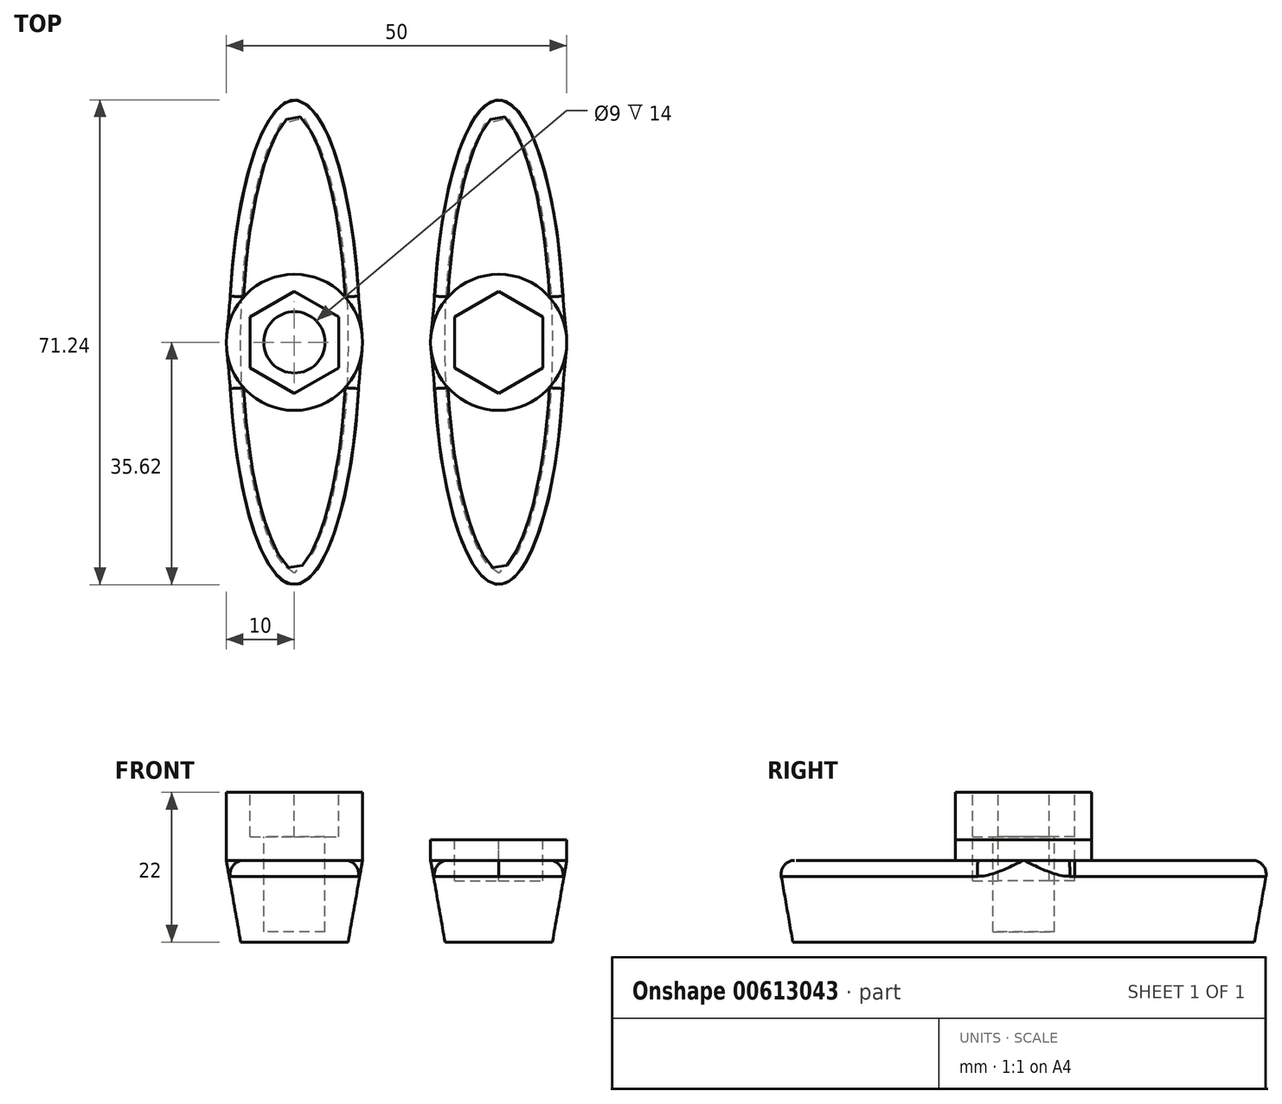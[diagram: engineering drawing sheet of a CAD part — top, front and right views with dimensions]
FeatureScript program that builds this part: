
annotation { "Feature Type Name" : "Feature", "Feature Type Description" : "" }
export const myFeature = defineFeature(function(context is Context, id is Id, definition is map)
    precondition{}
    {
        {
            var Q0;
            Q0=qCreatedBy(makeId("Top.planeOp"),FACE);
            var sketch = newSketch(context, id + "F0", { "sketchPlane" : qUnion([Q0])});
            skEllipse(sketch, "E0", {"center": v(0, 0) * mm, "majorRadius": 36 * mm, "minorRadius": 10 * mm, "majorAxis": v(0, 1)});
            skSolve(sketch);
        }
        {
            var Q0;
            Q0=makeQuery(id+"F0.imprint","IMPRINT",FACE,{"disambiguationData":[TD([[makeQuery(id+"F0.imprint","IMPRINT",EDGE,{"derivedFrom":sQuery(id+"F0.wireOp",EDGE,"E0")}),1.0]])]});
            extrude(context, id + "F1", {"entities" : qUnion([Q0]), "oppositeDirection" : true, "depth" : 12 * mm, "offsetDistance" : 25 * mm, "hasDraft" : true, "draftAngle" : 10 * degree, "draftPullDirection" : true});
        }
        {
            var Q0;
            Q0=makeQuery(id+"F1.opExtrude","SWEPT_BODY",BODY,{"disambiguationData":[OSD([sQuery(id+"F0.wireOp",EDGE,"E0")])]});
            transform(context, id + "F2", {"entities" : qUnion([Q0]), "transformType" : TransformType.TRANSLATION_3D, "dx" : 30 * mm, "dy" : 0 * mm, "dz" : 0 * mm, "makeCopy" : true});
        }
        {
            var Q0;
            Q0=makeQuery(id+"F1.opExtrude","CAP_FACE",FACE,{"disambiguationData":[OSD([sQuery(id+"F0.wireOp",EDGE,"E0")])],"isStart":true});
            var sketch = newSketch(context, id + "F3", { "sketchPlane" : qUnion([Q0])});
            skCircle(sketch, "E1", {"center": v(0, 0) * mm, "radius": 10 * mm});
            skSolve(sketch);
        }
        {
            var Q0;
            {var subQ0=sQuery(id+"F3.wireOp",EDGE,"E1");var subQ1=makeQuery(id+"F1.opExtrude","CAP_EDGE",EDGE,{"disambiguationData":[OSD([sQuery(id+"F0.wireOp",EDGE,"E0")])],"isStart":true});var subQ2=makeQuery(id+"F3.imprint","INTERSECT",VERTEX,{"disambiguationData":[OD(0.0)],"derivedFrom":[subQ1,subQ0]});Q0=makeQuery(id+"F3.imprint","IMPRINT",FACE,{"disambiguationData":[TD([[makeQuery(id+"F3.imprint","IMPRINT",EDGE,{"disambiguationData":[TD([[subQ2,1.0]])],"derivedFrom":subQ0}),1.0]])]});}
            extrude(context, id + "F4", {"entities" : qUnion([Q0]), "operationType" : NewBodyOperationType.ADD, "depth" : 10 * mm, "offsetDistance" : 25 * mm});
        }
        {
            var Q0;
            Q0=makeQuery(id+"F2.opPattern","COPY",FACE,{"derivedFrom":makeQuery(id+"F1.opExtrude","CAP_FACE",FACE,{"disambiguationData":[OSD([sQuery(id+"F0.wireOp",EDGE,"E0")])],"isStart":true}),"instanceName":"1"});
            var sketch = newSketch(context, id + "F5", { "sketchPlane" : qUnion([Q0])});
            skCircle(sketch, "E2", {"center": v(30, 0) * mm, "radius": 10 * mm});
            skSolve(sketch);
        }
        {
            var Q0;
            {var subQ0=sQuery(id+"F5.wireOp",EDGE,"E2");var subQ1=makeQuery(id+"F2.opPattern","COPY",EDGE,{"derivedFrom":makeQuery(id+"F1.opExtrude","CAP_EDGE",EDGE,{"disambiguationData":[OSD([sQuery(id+"F0.wireOp",EDGE,"E0")])],"isStart":true}),"instanceName":"1"});var subQ2=makeQuery(id+"F5.imprint","INTERSECT",VERTEX,{"disambiguationData":[OD(0.0)],"derivedFrom":[subQ1,subQ0]});Q0=makeQuery(id+"F5.imprint","IMPRINT",FACE,{"disambiguationData":[TD([[makeQuery(id+"F5.imprint","IMPRINT",EDGE,{"disambiguationData":[TD([[subQ2,1.0]])],"derivedFrom":subQ0}),1.0]])]});}
            extrude(context, id + "F6", {"entities" : qUnion([Q0]), "operationType" : NewBodyOperationType.ADD, "depth" : 3 * mm, "offsetDistance" : 25 * mm});
        }
        {
            var Q0;
            Q0=makeQuery(id+"F4.opExtrude","CAP_FACE",FACE,{"disambiguationData":[OSD([sQuery(id+"F3.wireOp",EDGE,"E1")])],"isStart":false});
            var sketch = newSketch(context, id + "F7", { "sketchPlane" : qUnion([Q0])});
            skCircle(sketch, "E3.cCircle", {"center": v(0, 0) * mm, "radius": 6.5 * mm, "construction": true});
            skLineSegment(sketch, "E3.0", {"start": v(6.5, 3.75) * mm, "end": v(6.5, -3.75) * mm});
            skLineSegment(sketch, "E3.1", {"start": v(6.5, -3.75) * mm, "end": v(0, -7.5) * mm});
            skLineSegment(sketch, "E3.2", {"start": v(0, -7.5) * mm, "end": v(-6.5, -3.75) * mm});
            skLineSegment(sketch, "E3.3", {"start": v(-6.5, -3.75) * mm, "end": v(-6.5, 3.75) * mm});
            skLineSegment(sketch, "E3.4", {"start": v(-6.5, 3.75) * mm, "end": v(0, 7.5) * mm});
            skLineSegment(sketch, "E3.5", {"start": v(0, 7.5) * mm, "end": v(6.5, 3.75) * mm});
            skPoint(sketch, "E3.0.midPoint", {"position": v(6.5, 0) * mm});
            skSolve(sketch);
        }
        {
            var Q0;
            Q0=makeQuery(id+"F7.imprint","IMPRINT",FACE,{"disambiguationData":[TD([[makeQuery(id+"F7.imprint","IMPRINT",EDGE,{"derivedFrom":sQuery(id+"F7.wireOp",EDGE,"E3.0")}),-1.0]])]});
            extrude(context, id + "F8", {"entities" : qUnion([Q0]), "operationType" : NewBodyOperationType.REMOVE, "oppositeDirection" : true, "depth" : 6.5 * mm, "offsetDistance" : 25 * mm});
        }
        {
            var Q0;
            Q0=makeQuery(id+"F8.boolean.opBoolean","COPY",FACE,{"derivedFrom":makeQuery(id+"F8.opExtrude","CAP_FACE",FACE,{"disambiguationData":[OSD([sQuery(id+"F7.wireOp",EDGE,"E3.0"),sQuery(id+"F7.wireOp",EDGE,"E3.1"),sQuery(id+"F7.wireOp",EDGE,"E3.2"),sQuery(id+"F7.wireOp",EDGE,"E3.3"),sQuery(id+"F7.wireOp",EDGE,"E3.4"),sQuery(id+"F7.wireOp",EDGE,"E3.5")])],"isStart":false})});
            var sketch = newSketch(context, id + "F9", { "sketchPlane" : qUnion([Q0])});
            skCircle(sketch, "E4", {"center": v(0, 0) * mm, "radius": 4.5 * mm});
            skSolve(sketch);
        }
        {
            var Q0;
            Q0=makeQuery(id+"F9.imprint","IMPRINT",FACE,{"disambiguationData":[TD([[makeQuery(id+"F9.imprint","IMPRINT",EDGE,{"derivedFrom":sQuery(id+"F9.wireOp",EDGE,"E4")}),1.0]])]});
            extrude(context, id + "F10", {"entities" : qUnion([Q0]), "operationType" : NewBodyOperationType.REMOVE, "oppositeDirection" : true, "depth" : 14 * mm, "offsetDistance" : 25 * mm});
        }
        {
            var Q0;
            Q0=makeQuery(id+"F6.opExtrude","CAP_FACE",FACE,{"disambiguationData":[OSD([sQuery(id+"F5.wireOp",EDGE,"E2")])],"isStart":false});
            var sketch = newSketch(context, id + "F11", { "sketchPlane" : qUnion([Q0])});
            skCircle(sketch, "E5.cCircle", {"center": v(30, 0) * mm, "radius": 6.5 * mm, "construction": true});
            skLineSegment(sketch, "E5.0", {"start": v(36.5, 3.75) * mm, "end": v(36.5, -3.75) * mm});
            skLineSegment(sketch, "E5.1", {"start": v(36.5, -3.75) * mm, "end": v(30, -7.5) * mm});
            skLineSegment(sketch, "E5.2", {"start": v(30, -7.5) * mm, "end": v(23.5, -3.75) * mm});
            skLineSegment(sketch, "E5.3", {"start": v(23.5, -3.75) * mm, "end": v(23.5, 3.75) * mm});
            skLineSegment(sketch, "E5.4", {"start": v(23.5, 3.75) * mm, "end": v(30, 7.5) * mm});
            skLineSegment(sketch, "E5.5", {"start": v(30, 7.5) * mm, "end": v(36.5, 3.75) * mm});
            skPoint(sketch, "E5.0.midPoint", {"position": v(36.5, 0) * mm});
            skSolve(sketch);
        }
        {
            var Q0;
            Q0=makeQuery(id+"F11.imprint","IMPRINT",FACE,{"disambiguationData":[TD([[makeQuery(id+"F11.imprint","IMPRINT",EDGE,{"derivedFrom":sQuery(id+"F11.wireOp",EDGE,"E5.0")}),-1.0]])]});
            extrude(context, id + "F12", {"entities" : qUnion([Q0]), "operationType" : NewBodyOperationType.REMOVE, "oppositeDirection" : true, "depth" : 6 * mm, "offsetDistance" : 25 * mm});
        }
        {
            var Q0;
            Q0=makeQuery(id+"F4.boolean.opBoolean","SPLIT",EDGE,{"disambiguationData":[OD(1.0)],"derivedFrom":makeQuery(id+"F1.opExtrude","CAP_EDGE",EDGE,{"disambiguationData":[OSD([sQuery(id+"F0.wireOp",EDGE,"E0")])],"isStart":true})});
            var Q1;
            Q1=makeQuery(id+"F6.boolean.opBoolean","SPLIT",EDGE,{"disambiguationData":[OD(0.0)],"derivedFrom":makeQuery(id+"F2.opPattern","COPY",EDGE,{"derivedFrom":makeQuery(id+"F1.opExtrude","CAP_EDGE",EDGE,{"disambiguationData":[OSD([sQuery(id+"F0.wireOp",EDGE,"E0")])],"isStart":true}),"instanceName":"1"})});
            fillet(context, id + "F13", {"entities" : qUnion([Q0, Q1]), "radius" : 2 * mm, "tangentPropagation" : true, "allowEdgeOverflow" : false});
        }
    });
